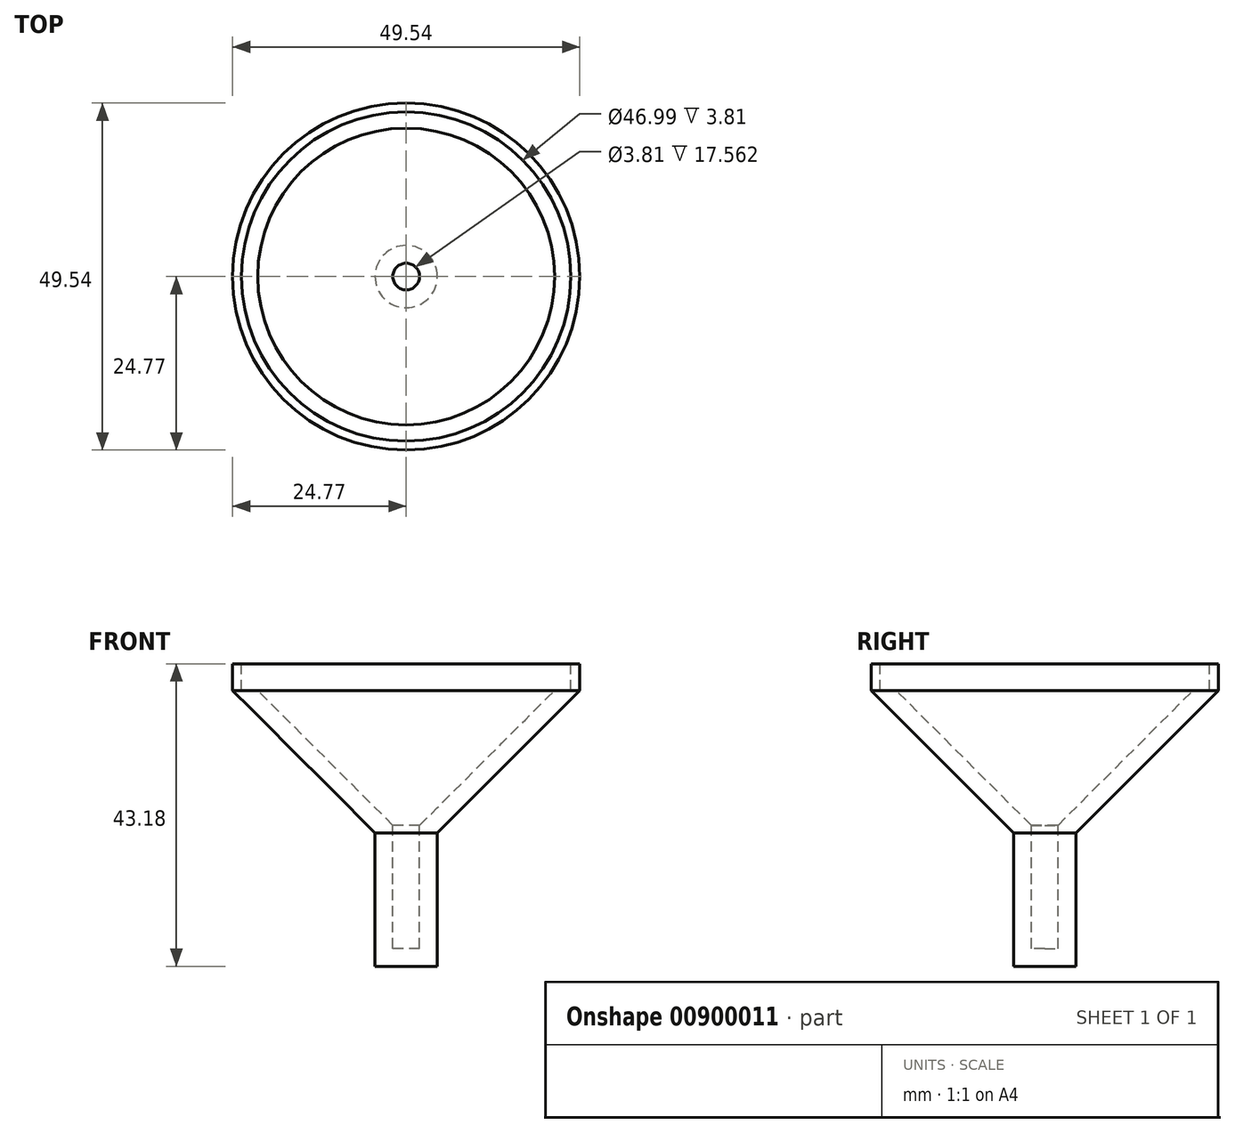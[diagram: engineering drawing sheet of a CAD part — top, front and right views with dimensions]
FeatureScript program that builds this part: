
annotation { "Feature Type Name" : "Feature", "Feature Type Description" : "" }
export const myFeature = defineFeature(function(context is Context, id is Id, definition is map)
    precondition{}
    {
        {
            var Q0;
            Q0=qCreatedBy(makeId("Top.planeOp"),FACE);
            var sketch = newSketch(context, id + "F0", { "sketchPlane" : qUnion([Q0])});
            skCircle(sketch, "E0", {"center": v(0, 0) * mm, "radius": 24.77 * mm});
            skSolve(sketch);
        }
        {
            var Q0;
            Q0=makeQuery(id+"F0.imprint","IMPRINT",FACE,{"disambiguationData":[TD([[makeQuery(id+"F0.imprint","IMPRINT",EDGE,{"derivedFrom":sQuery(id+"F0.wireOp",EDGE,"E0")}),1.0]])]});
            extrude(context, id + "F1", {"entities" : qUnion([Q0]), "depth" : 5.08 * mm, "offsetDistance" : 25.4 * mm});
        }
        {
            var Q0;
            Q0=makeQuery(id+"F1.opExtrude","CAP_FACE",FACE,{"disambiguationData":[OSD([sQuery(id+"F0.wireOp",EDGE,"E0")])],"isStart":false});
            var sketch = newSketch(context, id + "F2", { "sketchPlane" : qUnion([Q0])});
            skCircle(sketch, "E1", {"center": v(0, 0) * mm, "radius": 23.5 * mm});
            skCircle(sketch, "E2", {"center": v(0, 0) * mm, "radius": 20.32 * mm});
            skCircle(sketch, "E3", {"center": v(0, 0) * mm, "radius": 19.05 * mm});
            skSolve(sketch);
        }
        {
            var Q0;
            Q0=makeQuery(id+"F2.imprint","IMPRINT",FACE,{"disambiguationData":[TD([[makeQuery(id+"F2.imprint","IMPRINT",EDGE,{"derivedFrom":sQuery(id+"F2.wireOp",EDGE,"E1")}),1.0]])]});
            extrude(context, id + "F3", {"entities" : qUnion([Q0]), "operationType" : NewBodyOperationType.REMOVE, "oppositeDirection" : true, "depth" : 3.8 * mm, "offsetDistance" : 25.4 * mm});
        }
        {
            var Q0;
            Q0=makeQuery(id+"F1.opExtrude","CAP_FACE",FACE,{"disambiguationData":[OSD([sQuery(id+"F0.wireOp",EDGE,"E0")])],"isStart":true});
            var sketch = newSketch(context, id + "F4", { "sketchPlane" : qUnion([Q0])});
            skCircle(sketch, "E4", {"center": v(0, 0) * mm, "radius": 24.77 * mm});
            skSolve(sketch);
        }
        {
            var Q0;
            Q0 = qSketchRegion(id + "F4", true);
            extrude(context, id + "F5", {"entities" : qUnion([Q0]), "operationType" : NewBodyOperationType.ADD, "depth" : 19.05 * mm, "offsetDistance" : 25.4 * mm});
        }
        {
            var Q0;
            Q0=makeQuery(id+"F5.opExtrude","CAP_FACE",FACE,{"disambiguationData":[OSD([sQuery(id+"F4.wireOp",EDGE,"E4")])],"isStart":false});
            chamfer(context, id + "F6", {"entities" : qUnion([Q0]), "width" : 20.32 * mm, "tangentPropagation" : true});
        }
        {
            var Q0;
            Q0=makeQuery(id+"F5.opExtrude","CAP_FACE",FACE,{"disambiguationData":[OSD([sQuery(id+"F4.wireOp",EDGE,"E4")])],"isStart":false});
            var sketch = newSketch(context, id + "F7", { "sketchPlane" : qUnion([Q0])});
            skCircle(sketch, "E5", {"center": v(0, 0) * mm, "radius": 4.44 * mm});
            skSolve(sketch);
        }
        {
            var Q0;
            Q0 = qSketchRegion(id + "F7", true);
            extrude(context, id + "F8", {"entities" : qUnion([Q0]), "operationType" : NewBodyOperationType.ADD, "depth" : 19.05 * mm, "offsetDistance" : 25.4 * mm});
        }
        {
            var Q0;
            Q0=makeQuery(id+"F3.boolean.opBoolean","SPLIT",FACE,{"disambiguationData":[TD([makeQuery(id+"F3.opExtrude","SWEPT_FACE",FACE,{"disambiguationData":[OSD([sQuery(id+"F2.wireOp",EDGE,"E2")])]})])],"derivedFrom":makeQuery(id+"F1.opExtrude","CAP_FACE",FACE,{"disambiguationData":[OSD([sQuery(id+"F0.wireOp",EDGE,"E0")])],"isStart":false})});
            var sketch = newSketch(context, id + "F9", { "sketchPlane" : qUnion([Q0])});
            skCircle(sketch, "E6", {"center": v(0, 0) * mm, "radius": 20.32 * mm});
            skSolve(sketch);
        }
        {
            var Q0;
            Q0=makeQuery(id+"F9.imprint","IMPRINT",FACE,{"disambiguationData":[TD([[makeQuery(id+"F9.imprint","IMPRINT",EDGE,{"derivedFrom":sQuery(id+"F9.wireOp",EDGE,"E6")}),1.0]])]});
            extrude(context, id + "F10", {"entities" : qUnion([Q0]), "operationType" : NewBodyOperationType.REMOVE, "oppositeDirection" : true, "depth" : 3.8 * mm, "offsetDistance" : 25.4 * mm});
        }
        {
            var Q0;
            Q0=makeQuery(id+"F10.boolean.opBoolean","MERGE",FACE,{"derivedFrom":[makeQuery(id+"F3.boolean.opBoolean","COPY",FACE,{"derivedFrom":makeQuery(id+"F3.opExtrude","CAP_FACE",FACE,{"disambiguationData":[OSD([sQuery(id+"F2.wireOp",EDGE,"E1"),sQuery(id+"F2.wireOp",EDGE,"E2")])],"isStart":false})})],"fromTools":[makeQuery(id+"F10.opExtrude","CAP_FACE",FACE,{"disambiguationData":[OSD([sQuery(id+"F9.wireOp",EDGE,"E6")])],"isStart":false})]});
            shell(context, id + "F11", {"entities" : qUnion([Q0]), "thickness" : 2.54 * mm});
        }
    });
